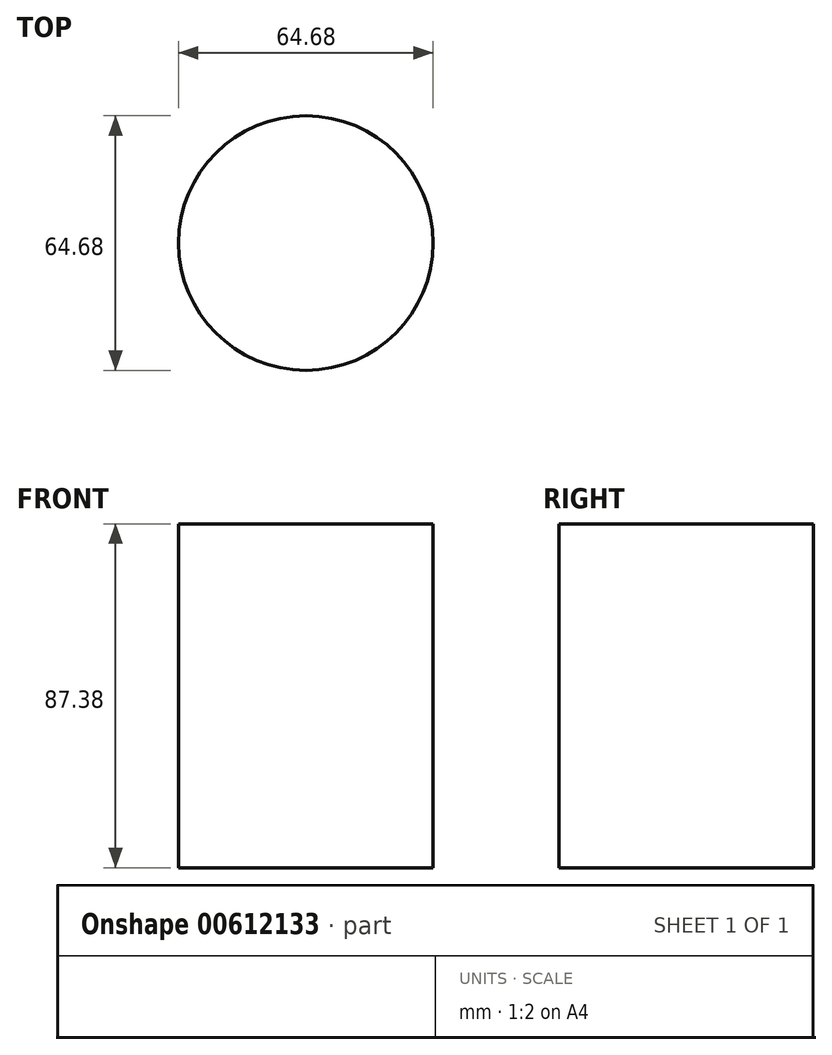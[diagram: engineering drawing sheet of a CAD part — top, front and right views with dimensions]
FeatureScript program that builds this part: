
annotation { "Feature Type Name" : "Feature", "Feature Type Description" : "" }
export const myFeature = defineFeature(function(context is Context, id is Id, definition is map)
    precondition{}
    {
        {
            var Q0;
            Q0=qCreatedBy(makeId("Front.planeOp"),FACE);
            var sketch = newSketch(context, id + "F0", { "sketchPlane" : qUnion([Q0])});
            skLineSegment(sketch, "E0.bottom", {"start": v(0, 38.9) * mm, "end": v(-32.34, 38.9) * mm});
            skLineSegment(sketch, "E0.top", {"start": v(0, -48.47) * mm, "end": v(-32.34, -48.47) * mm});
            skLineSegment(sketch, "E0.left", {"start": v(0, 38.9) * mm, "end": v(0, -48.47) * mm});
            skLineSegment(sketch, "E0.right", {"start": v(-32.34, 38.9) * mm, "end": v(-32.34, -48.47) * mm});
            skSolve(sketch);
        }
        {
            var Q0;
            Q0 = qSketchRegion(id + "F0", true);
            var Q1;
            Q1=sQuery(id+"F0.wireOp",EDGE,"E0.left");
            revolve(context, id + "F1", {"entities" : qUnion([Q0]), "axis" : qUnion([Q1]), "revolveType" : RevolveType.FULL});
        }
    });
